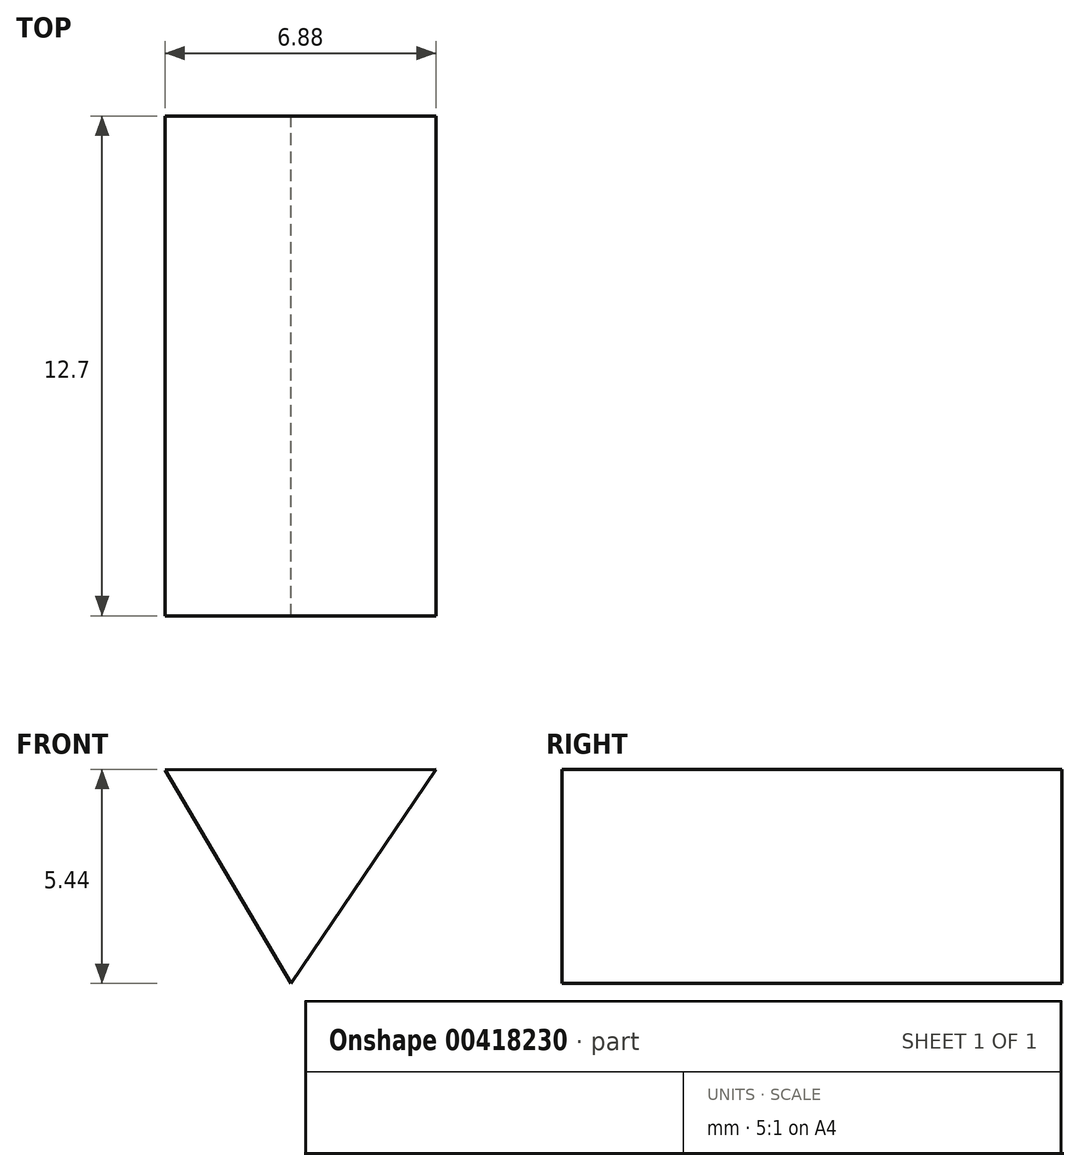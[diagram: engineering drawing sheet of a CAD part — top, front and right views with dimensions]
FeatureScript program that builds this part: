
annotation { "Feature Type Name" : "Feature", "Feature Type Description" : "" }
export const myFeature = defineFeature(function(context is Context, id is Id, definition is map)
    precondition{}
    {
        {
            var Q0;
            Q0=qCreatedBy(makeId("Front.planeOp"),FACE);
            var sketch = newSketch(context, id + "F0", { "sketchPlane" : qUnion([Q0])});
            skLineSegment(sketch, "E0", {"start": v(3.52, 1.82) * mm, "end": v(-0.17, -3.62) * mm});
            skLineSegment(sketch, "E1", {"start": v(-0.17, -3.62) * mm, "end": v(-3.36, 1.8) * mm});
            skLineSegment(sketch, "E2", {"start": v(-3.36, 1.8) * mm, "end": v(3.52, 1.82) * mm});
            skSolve(sketch);
        }
        {
            var Q0;
            Q0 = qSketchRegion(id + "F0", true);
            extrude(context, id + "F1", {"entities" : qUnion([Q0]), "depth" : 12.7 * mm});
        }
    });
